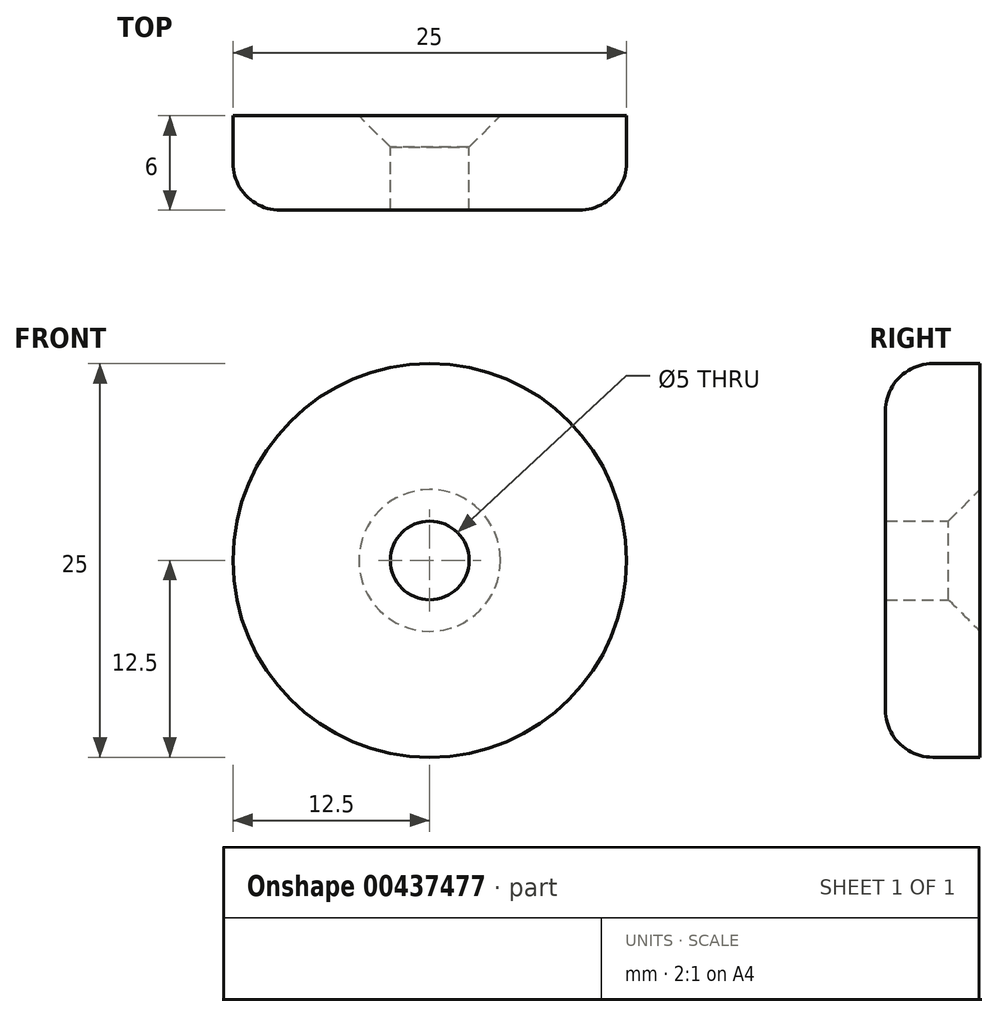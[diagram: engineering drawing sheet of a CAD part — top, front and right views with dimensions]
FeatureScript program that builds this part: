
annotation { "Feature Type Name" : "Feature", "Feature Type Description" : "" }
export const myFeature = defineFeature(function(context is Context, id is Id, definition is map)
    precondition{}
    {
        {
            var Q0;
            Q0=qCreatedBy(makeId("Front.planeOp"),FACE);
            var sketch = newSketch(context, id + "F0", { "sketchPlane" : qUnion([Q0])});
            skCircle(sketch, "E0", {"center": v(0, 0) * mm, "radius": 12.5 * mm});
            skCircle(sketch, "E1", {"center": v(0, 0) * mm, "radius": 2.5 * mm});
            skSolve(sketch);
        }
        {
            var Q0;
            Q0=makeQuery(id+"F0.imprint","IMPRINT",FACE,{"disambiguationData":[TD([[makeQuery(id+"F0.imprint","IMPRINT",EDGE,{"derivedFrom":sQuery(id+"F0.wireOp",EDGE,"E0")}),1.0]])]});
            extrude(context, id + "F1", {"entities" : qUnion([Q0]), "depth" : 6 * mm, "offsetDistance" : 25 * mm});
        }
        {
            var Q0;
            Q0=makeQuery(id+"F1.opExtrude","CAP_EDGE",EDGE,{"disambiguationData":[OSD([sQuery(id+"F0.wireOp",EDGE,"E0")])],"isStart":false});
            fillet(context, id + "F2", {"entities" : qUnion([Q0]), "tangentPropagation" : true, "radius" : 3 * mm, "defaultsChanged" : false, "vertexSettings" : [], "allowEdgeOverflow" : false});
        }
        {
            var Q0;
            Q0=makeQuery(id+"F1.opExtrude","CAP_EDGE",EDGE,{"disambiguationData":[OSD([sQuery(id+"F0.wireOp",EDGE,"E1")])],"isStart":true});
            chamfer(context, id + "F3", {"entities" : qUnion([Q0]), "width" : 2 * mm, "tangentPropagation" : true});
        }
    });
